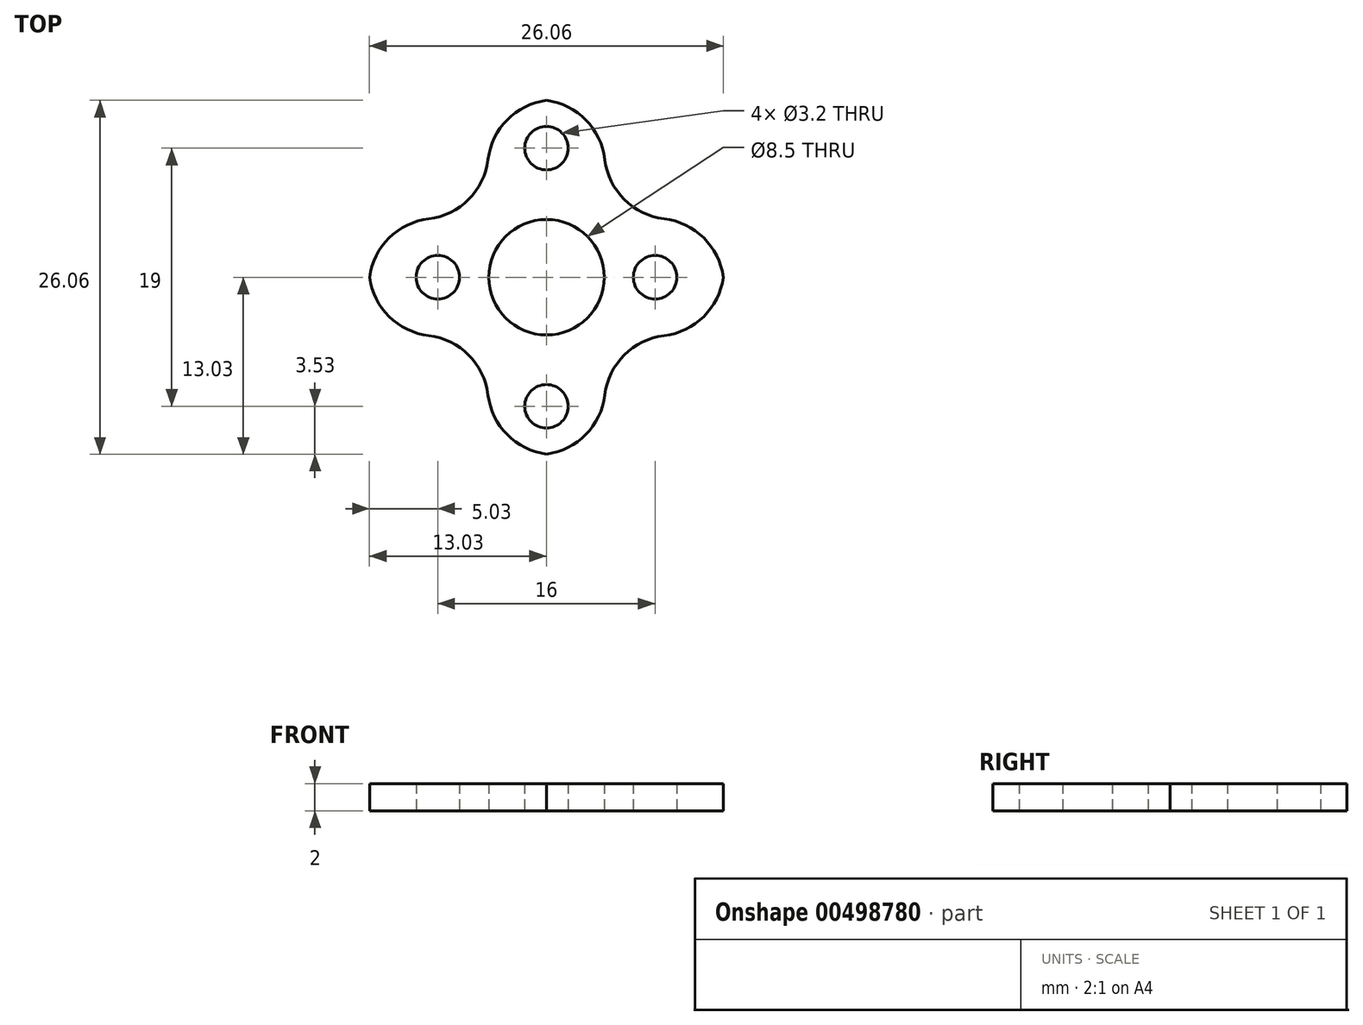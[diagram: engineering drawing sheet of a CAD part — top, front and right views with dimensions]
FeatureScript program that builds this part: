
annotation { "Feature Type Name" : "Feature", "Feature Type Description" : "" }
export const myFeature = defineFeature(function(context is Context, id is Id, definition is map)
    precondition{}
    {
        {
            assignVariable(context, id + "F0", {"name" : "thickness", "anyValue" : 2 * mm});
        }
        {
            var Q0;
            Q0=qCreatedBy(makeId("Top.planeOp"),FACE);
            var sketch = newSketch(context, id + "F1", { "sketchPlane" : qUnion([Q0])});
            skCircle(sketch, "E0", {"center": v(0, 0) * mm, "radius": 13.1 * mm});
            skLineSegment(sketch, "E1", {"start": v(0, 9.5) * mm, "end": v(0, 0) * mm});
            skLineSegment(sketch, "E2", {"start": v(0, 0) * mm, "end": v(0, -9.5) * mm});
            skLineSegment(sketch, "E3", {"start": v(-8, 0) * mm, "end": v(0, 0) * mm});
            skLineSegment(sketch, "E4", {"start": v(0, 0) * mm, "end": v(8, 0) * mm});
            skCircle(sketch, "E5", {"center": v(0, 9.5) * mm, "radius": 1.6 * mm});
            skCircle(sketch, "E6", {"center": v(8, 0) * mm, "radius": 1.6 * mm});
            skCircle(sketch, "E7", {"center": v(0, -9.5) * mm, "radius": 1.6 * mm});
            skCircle(sketch, "E8", {"center": v(-8, 0) * mm, "radius": 1.6 * mm});
            skCircle(sketch, "E9", {"center": v(0, 0) * mm, "radius": 4.25 * mm});
            skSolve(sketch);
        }
        {
            var Q0;
            Q0 = qSketchRegion(id + "F1", true);
            extrude(context, id + "F2", {"entities" : qUnion([Q0]), "depth" : getVariable(context, 'thickness')});
        }
        {
            var Q0;
            Q0=makeQuery(id+"F2.opExtrude","CAP_FACE",FACE,{"disambiguationData":[OSD([sQuery(id+"F1.wireOp",EDGE,"E0"),sQuery(id+"F1.wireOp",EDGE,"E5"),sQuery(id+"F1.wireOp",EDGE,"E6"),sQuery(id+"F1.wireOp",EDGE,"E7"),sQuery(id+"F1.wireOp",EDGE,"E8"),sQuery(id+"F1.wireOp",EDGE,"E9")])],"isStart":false});
            var sketch = newSketch(context, id + "F3", { "sketchPlane" : qUnion([Q0])});
            skLineSegment(sketch, "E10", {"start": v(0, 0) * mm, "end": v(-9.26, 9.26) * mm, "construction": true});
            skLineSegment(sketch, "E11", {"start": v(0, 0) * mm, "end": v(9.26, 9.26) * mm, "construction": true});
            skLineSegment(sketch, "E12", {"start": v(0, 0) * mm, "end": v(9.26, -9.26) * mm, "construction": true});
            skLineSegment(sketch, "E13", {"start": v(0, 0) * mm, "end": v(-9.26, -9.26) * mm, "construction": true});
            skCircle(sketch, "E14", {"center": v(-9.26, 9.26) * mm, "radius": 5 * mm});
            skCircle(sketch, "E15", {"center": v(9.26, -9.26) * mm, "radius": 5 * mm});
            skCircle(sketch, "E16", {"center": v(-9.26, -9.26) * mm, "radius": 5 * mm});
            skCircle(sketch, "E17", {"center": v(9.26, 9.26) * mm, "radius": 5 * mm});
            skSolve(sketch);
        }
        {
            var Q0;
            Q0 = qSketchRegion(id + "F3", true);
            extrude(context, id + "F4", {"entities" : qUnion([Q0]), "operationType" : NewBodyOperationType.REMOVE, "oppositeDirection" : true, "depth" : 25 * mm});
        }
        {
            var Q0;
            Q0=makeQuery(id+"F4.boolean.opBoolean","INTERSECT",EDGE,{"disambiguationData":[OD(1.0)],"derivedFrom":[makeQuery(id+"F2.opExtrude","SWEPT_FACE",FACE,{"disambiguationData":[OSD([sQuery(id+"F1.wireOp",EDGE,"E0")])]}),makeQuery(id+"F4.opExtrude","SWEPT_FACE",FACE,{"disambiguationData":[OSD([sQuery(id+"F3.wireOp",EDGE,"E14")])]})]});
            var Q1;
            Q1=makeQuery(id+"F4.boolean.opBoolean","INTERSECT",EDGE,{"disambiguationData":[OD(0.0)],"derivedFrom":[makeQuery(id+"F2.opExtrude","SWEPT_FACE",FACE,{"disambiguationData":[OSD([sQuery(id+"F1.wireOp",EDGE,"E0")])]}),makeQuery(id+"F4.opExtrude","SWEPT_FACE",FACE,{"disambiguationData":[OSD([sQuery(id+"F3.wireOp",EDGE,"E17")])]})]});
            var Q2;
            Q2=makeQuery(id+"F4.boolean.opBoolean","INTERSECT",EDGE,{"disambiguationData":[OD(1.0)],"derivedFrom":[makeQuery(id+"F2.opExtrude","SWEPT_FACE",FACE,{"disambiguationData":[OSD([sQuery(id+"F1.wireOp",EDGE,"E0")])]}),makeQuery(id+"F4.opExtrude","SWEPT_FACE",FACE,{"disambiguationData":[OSD([sQuery(id+"F3.wireOp",EDGE,"E17")])]})]});
            var Q3;
            Q3=makeQuery(id+"F4.boolean.opBoolean","INTERSECT",EDGE,{"disambiguationData":[OD(1.0)],"derivedFrom":[makeQuery(id+"F2.opExtrude","SWEPT_FACE",FACE,{"disambiguationData":[OSD([sQuery(id+"F1.wireOp",EDGE,"E0")])]}),makeQuery(id+"F4.opExtrude","SWEPT_FACE",FACE,{"disambiguationData":[OSD([sQuery(id+"F3.wireOp",EDGE,"E15")])]})]});
            var Q4;
            Q4=makeQuery(id+"F4.boolean.opBoolean","INTERSECT",EDGE,{"disambiguationData":[OD(0.0)],"derivedFrom":[makeQuery(id+"F2.opExtrude","SWEPT_FACE",FACE,{"disambiguationData":[OSD([sQuery(id+"F1.wireOp",EDGE,"E0")])]}),makeQuery(id+"F4.opExtrude","SWEPT_FACE",FACE,{"disambiguationData":[OSD([sQuery(id+"F3.wireOp",EDGE,"E15")])]})]});
            var Q5;
            Q5=makeQuery(id+"F4.boolean.opBoolean","INTERSECT",EDGE,{"disambiguationData":[OD(1.0)],"derivedFrom":[makeQuery(id+"F2.opExtrude","SWEPT_FACE",FACE,{"disambiguationData":[OSD([sQuery(id+"F1.wireOp",EDGE,"E0")])]}),makeQuery(id+"F4.opExtrude","SWEPT_FACE",FACE,{"disambiguationData":[OSD([sQuery(id+"F3.wireOp",EDGE,"E16")])]})]});
            var Q6;
            Q6=makeQuery(id+"F4.boolean.opBoolean","INTERSECT",EDGE,{"disambiguationData":[OD(0.0)],"derivedFrom":[makeQuery(id+"F2.opExtrude","SWEPT_FACE",FACE,{"disambiguationData":[OSD([sQuery(id+"F1.wireOp",EDGE,"E0")])]}),makeQuery(id+"F4.opExtrude","SWEPT_FACE",FACE,{"disambiguationData":[OSD([sQuery(id+"F3.wireOp",EDGE,"E16")])]})]});
            var Q7;
            Q7=makeQuery(id+"F4.boolean.opBoolean","INTERSECT",EDGE,{"disambiguationData":[OD(0.0)],"derivedFrom":[makeQuery(id+"F2.opExtrude","SWEPT_FACE",FACE,{"disambiguationData":[OSD([sQuery(id+"F1.wireOp",EDGE,"E0")])]}),makeQuery(id+"F4.opExtrude","SWEPT_FACE",FACE,{"disambiguationData":[OSD([sQuery(id+"F3.wireOp",EDGE,"E14")])]})]});
            fillet(context, id + "F5", {"entities" : qUnion([Q0, Q1, Q2, Q3, Q4, Q5, Q6, Q7]), "radius" : 5 * mm, "tangentPropagation" : true, "allowEdgeOverflow" : false});
        }
    });
